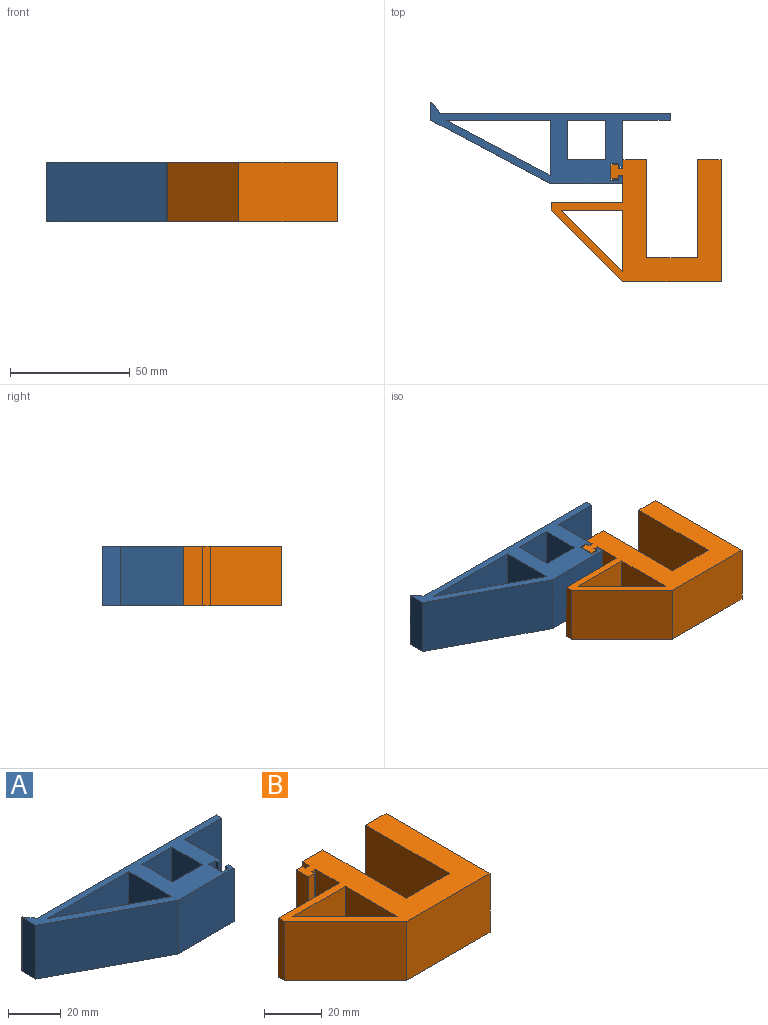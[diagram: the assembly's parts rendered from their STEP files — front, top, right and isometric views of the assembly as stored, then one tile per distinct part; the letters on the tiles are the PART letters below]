
ASSEMBLY  parts=2 mates=1
PART A: 26 faces, bbox 100x34.1x25 mm
  f0: plane 25x16.5mm, normal (1,0,0), area 412.5mm2, adj f1,f23,f24,f25
  f1: plane 25x16mm, normal (0,-1,0), area 400mm2, adj f0,f2,f24,f25
  f2: plane 25x16.5mm, normal (-1,0,0), area 412.5mm2, adj f1,f23,f24,f25
  f3: plane 43.59x25mm, normal (0.47,0.88,0), area 1233.5mm2, adj f4,f21,f24,f25
  f4: plane 43.59x25mm, normal (0,-1,0), area 1089.8mm2, adj f3,f21,f24,f25
  f5: plane 25x7.4mm, normal (-1,0,0), area 185mm2, adj f6,f22,f24,f25
  f6: plane 50x26.5mm, normal (-0.47,-0.88,0), area 1414.7mm2, adj f5,f7,f24,f25
  f7: plane 30x25mm, normal (0,-1,0), area 750mm2, adj f6,f8,f24,f25
  f8: plane 25x3.15mm, normal (1,0,0), area 78.7mm2, adj f7,f9,f24,f25
  f9: plane 25x1.5mm, normal (0,1,0), area 37.5mm2, adj f8,f10,f24,f25
  f10: plane 25x1.65mm, normal (-1,0,0), area 41.2mm2, adj f9,f11,f24,f25
  f11: plane 25x3.5mm, normal (0,1,0), area 87.5mm2, adj f10,f12,f24,f25
  f12: plane 25x7mm, normal (1,0,0), area 175mm2, adj f11,f13,f24,f25
  f13: plane 25x3.5mm, normal (0,-1,0), area 87.5mm2, adj f12,f14,f24,f25
  f14: plane 25x1.65mm, normal (-1,0,0), area 41.3mm2, adj f13,f15,f24,f25
  f15: plane 25x1.5mm, normal (0,-1,0), area 37.5mm2, adj f14,f16,f24,f25
  f16: plane 25x19.65mm, normal (1,0,0), area 491.2mm2, adj f15,f17,f24,f25
  f17: plane 25x20mm, normal (0,-1,0), area 500mm2, adj f16,f18,f24,f25
  f18: plane 25x3mm, normal (1,0,0), area 75mm2, adj f17,f19,f24,f25
  f19: plane 96.24x25mm, normal (0,1,0), area 2406mm2, adj f18,f20,f24,f25
  f20: plane 25x4.52mm, normal (0.8,0.6,0), area 141.4mm2, adj f19,f22,f24,f25
  f21: plane 25x23.1mm, normal (-1,0,0), area 577.6mm2, adj f3,f4,f24,f25
  f22: cylinder r=0.2mm len=25mm, axis (0,0,-1), area 12.5mm2, adj f5,f20,f24,f25
  f23: plane 25x16mm, normal (0,1,0), area 400mm2, adj f0,f2,f24,f25
  f24: plane 100x34.1mm, normal (0,0,1), area 969.2mm2, adj f0,f1,f2,f3,f4,f5,f6,f7
  f25: plane 100x34.1mm, normal (0,0,-1), area 969.2mm2, adj f0,f1,f2,f3,f4,f5,f6,f7
PART B: 24 faces, bbox 71x51x25 mm
  f0: plane 25.76x25mm, normal (0,-1,0), area 643.9mm2, adj f1,f21,f22,f23
  f1: plane 25.76x25mm, normal (-1,0,0), area 643.9mm2, adj f0,f21,f22,f23
  f2: plane 25x1.5mm, normal (1,0,0), area 37.5mm2, adj f3,f20,f22,f23
  f3: plane 25x2mm, normal (0,-1,0), area 50mm2, adj f2,f4,f22,f23
  f4: plane 25x11.5mm, normal (-1,0,0), area 287.5mm2, adj f3,f5,f22,f23
  f5: plane 30x25mm, normal (0,1,0), area 750mm2, adj f4,f6,f22,f23
  f6: plane 25x3mm, normal (-1,0,0), area 75mm2, adj f5,f7,f22,f23
  f7: plane 30x30mm, normal (-0.71,-0.71,0), area 1060.7mm2, adj f6,f8,f22,f23
  f8: plane 41x25mm, normal (0,-1,0), area 1025mm2, adj f7,f9,f22,f23
  f9: plane 51x25mm, normal (1,0,0), area 1275mm2, adj f8,f10,f22,f23
  f10: plane 25x10mm, normal (0,1,0), area 250mm2, adj f9,f11,f22,f23
  f11: plane 41x25mm, normal (-1,0,0), area 1025mm2, adj f10,f12,f22,f23
  f12: plane 25x21mm, normal (0,1,0), area 525mm2, adj f11,f13,f22,f23
  f13: plane 41x25mm, normal (1,0,0), area 1025mm2, adj f12,f14,f22,f23
  f14: plane 25x10mm, normal (0,1,0), area 250mm2, adj f13,f15,f22,f23
  f15: plane 25x3.5mm, normal (-1,0,0), area 87.5mm2, adj f14,f16,f22,f23
  f16: plane 25x2mm, normal (0,1,0), area 50mm2, adj f15,f17,f22,f23
  f17: plane 25x1.5mm, normal (1,0,0), area 37.5mm2, adj f16,f18,f22,f23
  f18: plane 25x3mm, normal (0,1,0), area 75mm2, adj f17,f19,f22,f23
  f19: plane 25x6mm, normal (-1,0,0), area 150mm2, adj f18,f20,f22,f23
  f20: plane 25x3mm, normal (0,-1,0), area 75mm2, adj f2,f19,f22,f23
  f21: plane 25.76x25.76mm, normal (0.71,0.71,0), area 910.7mm2, adj f0,f1,f22,f23
  f22: plane 71x51mm, normal (0,0,1), area 1462.3mm2, adj f0,f1,f2,f3,f4,f5,f6,f7
  f23: plane 71x51mm, normal (0,0,-1), area 1462.3mm2, adj f0,f1,f2,f3,f4,f5,f6,f7
PLACE A t=(-9.06,2.97,0)mm
PLACE B t=(-21.17,2.78,0)mm
MATE parallel B.f19 <-> A.f12  axis (-1,0,0) through (-13.81,7.97,12.5)mm
